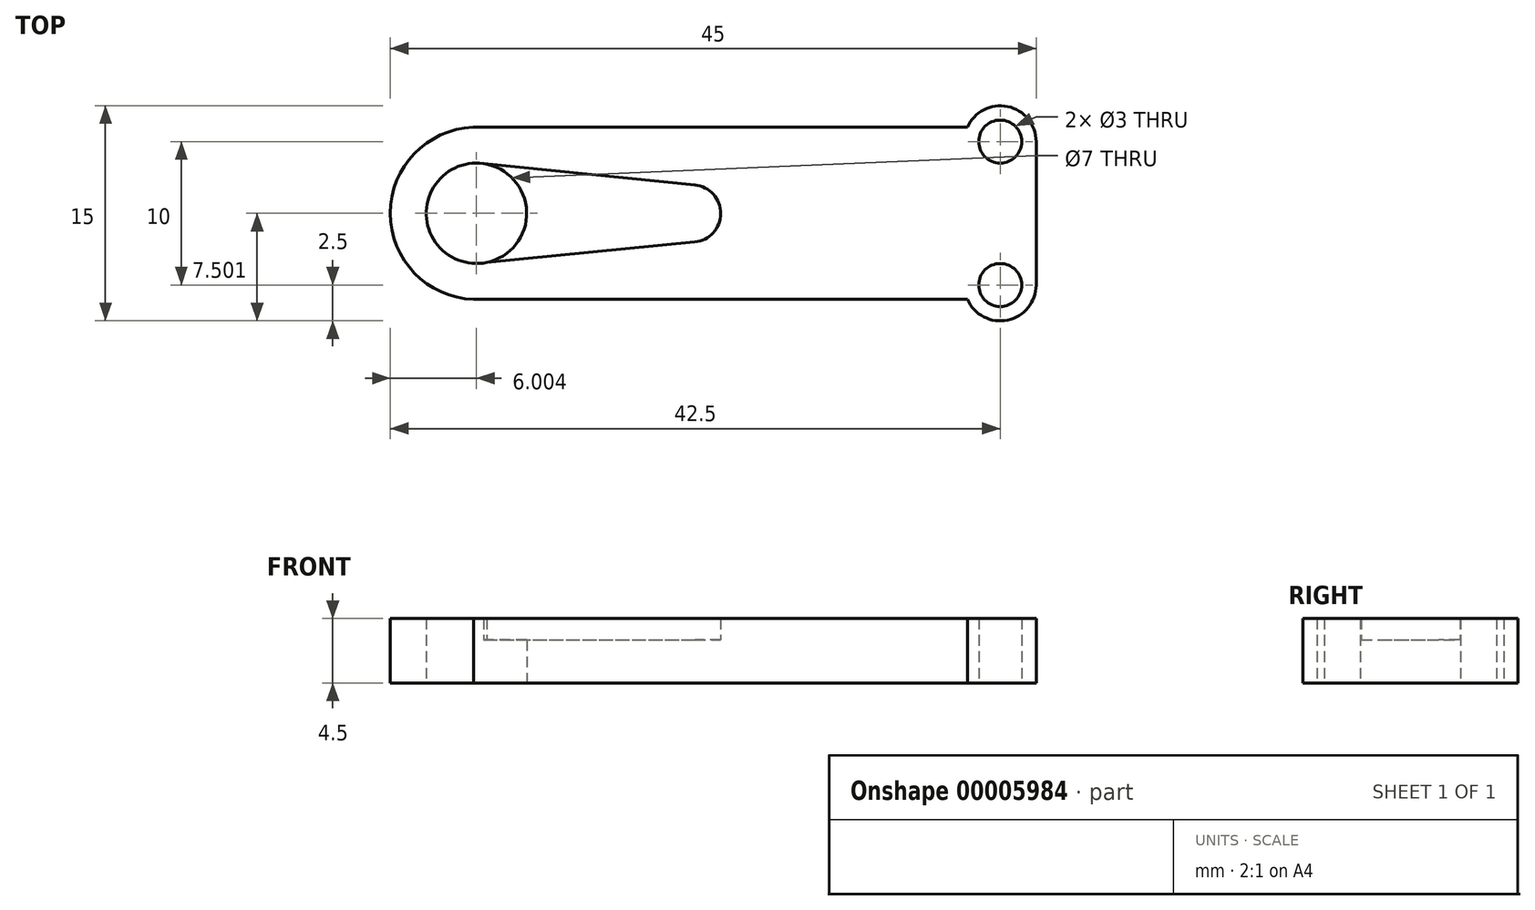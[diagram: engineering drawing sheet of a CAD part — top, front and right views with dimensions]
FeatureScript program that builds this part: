
annotation { "Feature Type Name" : "Feature", "Feature Type Description" : "" }
export const myFeature = defineFeature(function(context is Context, id is Id, definition is map)
    precondition{}
    {
        {
            var Q0;
            Q0=qCreatedBy(makeId("Top.planeOp"),FACE);
            var sketch = newSketch(context, id + "F0", { "sketchPlane" : qUnion([Q0])});
            skLineSegment(sketch, "E0.bottom", {"start": v(5.8, 0) * mm, "end": v(40.2, 0) * mm});
            skLineSegment(sketch, "E0.top", {"start": v(5.76, 12) * mm, "end": v(40.2, 12) * mm});
            skLineSegment(sketch, "E0.left", {"start": v(0, 6) * mm, "end": v(0, 6) * mm});
            skArc(sketch, "E1", {"start": v(6.25, 12) * mm, "mid": v(0, 6.02) * mm, "end": v(6.22, 0) * mm});
            skPoint(sketch, "E1.first.point", {"position": v(6.25, 12) * mm});
            skPoint(sketch, "E1.second.point", {"position": v(0, 6) * mm});
            skPoint(sketch, "E1.third.point", {"position": v(6.22, 0) * mm});
            skCircle(sketch, "E2", {"center": v(6, 6) * mm, "radius": 3.5 * mm});
            skPoint(sketch, "E3.orphan", {"position": v(0, 0) * mm});
            skPoint(sketch, "E4.orphan", {"position": v(0, 12) * mm});
            skLineSegment(sketch, "E5.top", {"start": v(6, 9.5) * mm, "end": v(6.22, 9.5) * mm});
            skArc(sketch, "E6", {"start": v(21.21, 4) * mm, "mid": v(23.02, 5.98) * mm, "end": v(21.22, 7.98) * mm});
            skLineSegment(sketch, "E7", {"start": v(5.97, 2.5) * mm, "end": v(21.21, 4) * mm});
            skLineSegment(sketch, "E8", {"start": v(6.22, 9.5) * mm, "end": v(21.22, 7.98) * mm});
            skLineSegment(sketch, "E9", {"start": v(45, 11) * mm, "end": v(45, 1) * mm});
            skCircle(sketch, "E10", {"center": v(42.5, 11) * mm, "radius": 1.5 * mm});
            skCircle(sketch, "E11", {"center": v(42.5, 1) * mm, "radius": 1.5 * mm});
            skArc(sketch, "E12.0", {"start": v(45, 11) * mm, "mid": v(43.01, 13.45) * mm, "end": v(40.2, 12) * mm});
            skArc(sketch, "E13.0", {"start": v(40.2, 0) * mm, "mid": v(43.01, -1.45) * mm, "end": v(45, 1) * mm});
            skSolve(sketch);
        }
        {
            var Q0;
            {var subQ4=sQuery(id+"F0.wireOp",EDGE,"E6");Q0=makeQuery(id+"F0.imprint","IMPRINT",FACE,{"disambiguationData":[TD([[makeQuery(id+"F0.imprint","IMPRINT",EDGE,{"derivedFrom":subQ4}),-1.0]])]});}
            extrude(context, id + "F1", {"entities" : qUnion([Q0]), "depth" : 4.5 * mm});
        }
        {
            var Q0;
            {var subQ3=sQuery(id+"F0.wireOp",EDGE,"E6");Q0=makeQuery(id+"F0.imprint","IMPRINT",FACE,{"disambiguationData":[TD([[makeQuery(id+"F0.imprint","IMPRINT",EDGE,{"derivedFrom":subQ3}),1.0]])]});}
            extrude(context, id + "F2", {"entities" : qUnion([Q0]), "operationType" : NewBodyOperationType.ADD, "depth" : 3 * mm});
        }
    });
